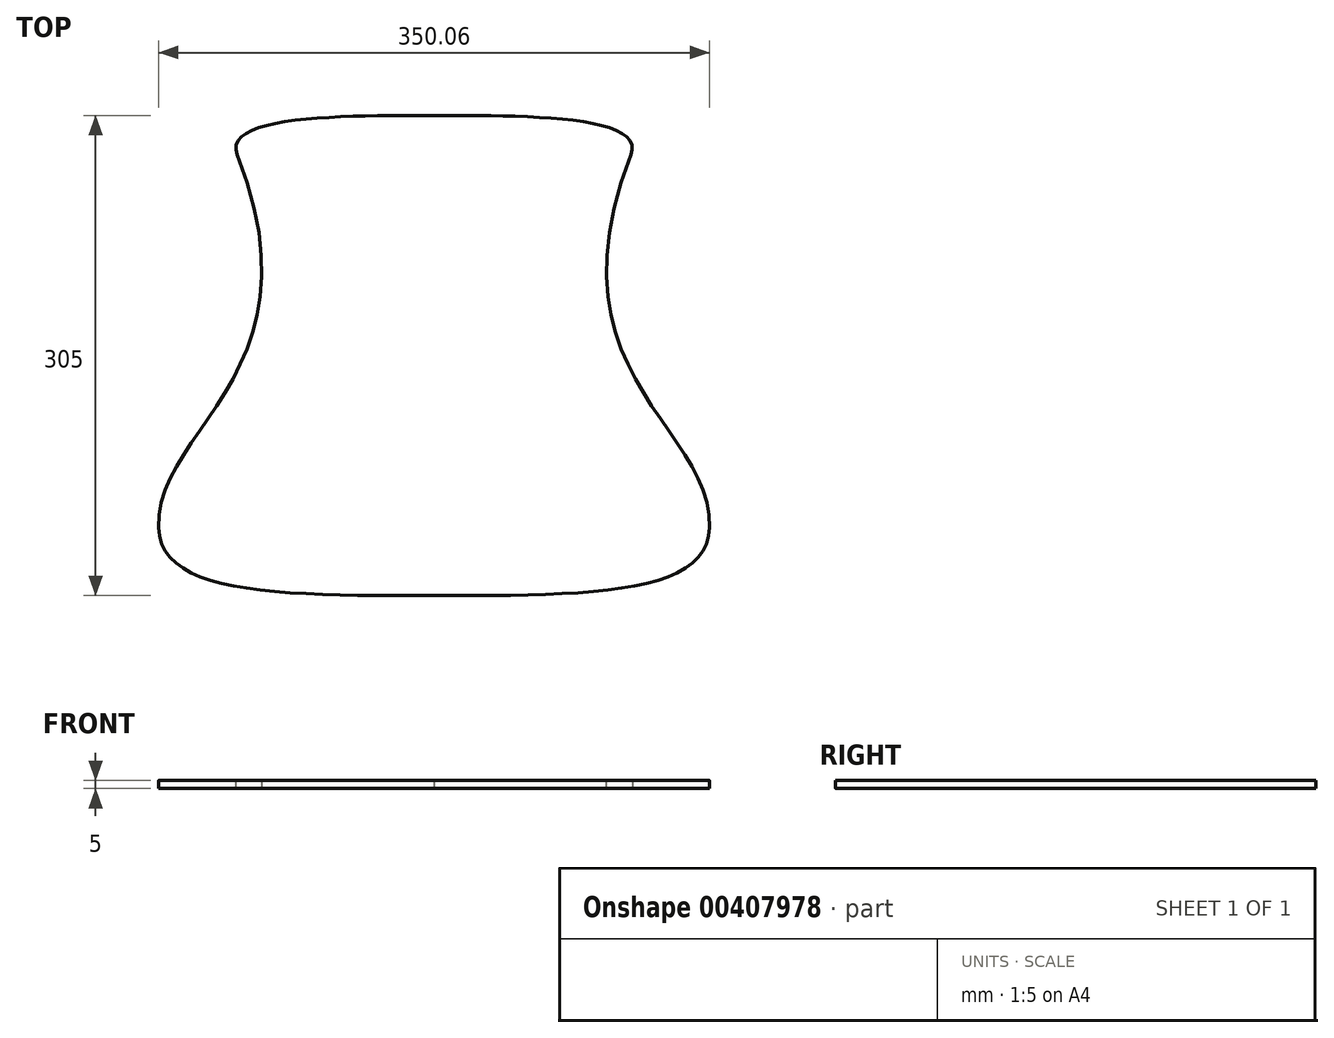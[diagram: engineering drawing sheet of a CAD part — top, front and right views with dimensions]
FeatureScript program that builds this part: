
annotation { "Feature Type Name" : "Feature", "Feature Type Description" : "" }
export const myFeature = defineFeature(function(context is Context, id is Id, definition is map)
    precondition{}
    {
        {
            var Q0;
            Q0=qCreatedBy(makeId("Top.planeOp"),FACE);
            var sketch = newSketch(context, id + "F0", { "sketchPlane" : qUnion([Q0])});
            skLineSegment(sketch, "E0.bottom", {"start": v(-125, 0) * mm, "end": v(125, 0) * mm, "construction": true});
            skLineSegment(sketch, "E0.top", {"start": v(-125, -280) * mm, "end": v(125, -280) * mm, "construction": true});
            skLineSegment(sketch, "E0.left", {"start": v(-125, 0) * mm, "end": v(-125, -280) * mm, "construction": true});
            skLineSegment(sketch, "E0.right", {"start": v(125, 0) * mm, "end": v(125, -280) * mm, "construction": true});
            skFitSpline(sketch, "E1", {"points": [v(-125, 0) * mm, v(-175, -236.88) * mm], "startDerivative": vector(163.58, -419.06) * mm, "endDerivative": vector(5.98, -192.46) * mm});
            skPoint(sketch, "E2", {"position": v(0, -280) * mm});
            skFitSpline(sketch, "E3", {"points": [v(-175, -236.88) * mm, v(0, -280) * mm], "startDerivative": vector(4.02, -129.37) * mm, "endDerivative": vector(290.73, 0) * mm});
            skFitSpline(sketch, "E4.MirrorCS", {"points": [v(125, 0) * mm, v(175, -236.88) * mm], "startDerivative": vector(-163.58, -419.06) * mm, "endDerivative": vector(-5.98, -192.46) * mm});
            skFitSpline(sketch, "E5.MirrorCS", {"points": [v(175, -236.88) * mm, v(0, -280) * mm], "startDerivative": vector(-4.02, -129.37) * mm, "endDerivative": vector(-290.73, 0) * mm});
            skFitSpline(sketch, "E6", {"points": [v(-125, 0) * mm, v(0, 25) * mm], "startDerivative": vector(-31, 79.42) * mm, "endDerivative": vector(148.36, 0.98) * mm});
            skFitSpline(sketch, "E7.MirrorCS", {"points": [v(125, 0) * mm, v(0, 25) * mm], "startDerivative": vector(31, 79.42) * mm, "endDerivative": vector(-148.36, 0.98) * mm});
            skLineSegment(sketch, "E8.bottom", {"start": v(-10, -88) * mm, "end": v(-5, -88) * mm, "construction": true});
            skLineSegment(sketch, "E8.top", {"start": v(-10, -278) * mm, "end": v(-5, -278) * mm, "construction": true});
            skLineSegment(sketch, "E8.left", {"start": v(-10, -88) * mm, "end": v(-10, -278) * mm, "construction": true});
            skLineSegment(sketch, "E8.right", {"start": v(-5, -88) * mm, "end": v(-5, -278) * mm, "construction": true});
            skLineSegment(sketch, "E9.1.0.0", {"start": v(-20, -88) * mm, "end": v(-20, -278) * mm, "construction": true});
            skLineSegment(sketch, "E9.1.0.1", {"start": v(-15, -88) * mm, "end": v(-15, -278) * mm, "construction": true});
            skLineSegment(sketch, "E9.1.0.2", {"start": v(-20, -88) * mm, "end": v(-15, -88) * mm, "construction": true});
            skLineSegment(sketch, "E9.1.0.3", {"start": v(-20, -278) * mm, "end": v(-15, -278) * mm, "construction": true});
            skLineSegment(sketch, "E9.2.0.0", {"start": v(-30, -88) * mm, "end": v(-30, -278) * mm, "construction": true});
            skLineSegment(sketch, "E9.2.0.1", {"start": v(-25, -88) * mm, "end": v(-25, -278) * mm, "construction": true});
            skLineSegment(sketch, "E9.2.0.2", {"start": v(-30, -88) * mm, "end": v(-25, -88) * mm, "construction": true});
            skLineSegment(sketch, "E9.2.0.3", {"start": v(-30, -278) * mm, "end": v(-25, -278) * mm, "construction": true});
            skLineSegment(sketch, "E9.direction1", {"start": v(-10, -278) * mm, "end": v(-20, -278) * mm, "construction": true});
            skLineSegment(sketch, "E10.MirrorCS", {"start": v(10, -278) * mm, "end": v(20, -278) * mm, "construction": true});
            skLineSegment(sketch, "E11.MirrorCS", {"start": v(20, -278) * mm, "end": v(15, -278) * mm, "construction": true});
            skLineSegment(sketch, "E12.MirrorCS", {"start": v(10, -278) * mm, "end": v(5, -278) * mm, "construction": true});
            skLineSegment(sketch, "E13.MirrorCS", {"start": v(20, -88) * mm, "end": v(15, -88) * mm, "construction": true});
            skLineSegment(sketch, "E14.MirrorCS", {"start": v(30, -278) * mm, "end": v(25, -278) * mm, "construction": true});
            skLineSegment(sketch, "E15.MirrorCS", {"start": v(10, -88) * mm, "end": v(5, -88) * mm, "construction": true});
            skLineSegment(sketch, "E16.MirrorCS", {"start": v(30, -88) * mm, "end": v(25, -88) * mm, "construction": true});
            skLineSegment(sketch, "E17.MirrorCS", {"start": v(30, -88) * mm, "end": v(30, -278) * mm, "construction": true});
            skLineSegment(sketch, "E18.MirrorCS", {"start": v(10, -88) * mm, "end": v(10, -278) * mm, "construction": true});
            skLineSegment(sketch, "E19.MirrorCS", {"start": v(15, -88) * mm, "end": v(15, -278) * mm, "construction": true});
            skLineSegment(sketch, "E20.MirrorCS", {"start": v(5, -88) * mm, "end": v(5, -278) * mm, "construction": true});
            skLineSegment(sketch, "E21.MirrorCS", {"start": v(20, -88) * mm, "end": v(20, -278) * mm, "construction": true});
            skLineSegment(sketch, "E22.MirrorCS", {"start": v(25, -88) * mm, "end": v(25, -278) * mm, "construction": true});
            skLineSegment(sketch, "E23.bottom", {"start": v(-73, -5) * mm, "end": v(-57, -5) * mm, "construction": true});
            skLineSegment(sketch, "E23.top", {"start": v(-73, -18) * mm, "end": v(-57, -18) * mm, "construction": true});
            skLineSegment(sketch, "E23.left", {"start": v(-73, -5) * mm, "end": v(-73, -18) * mm, "construction": true});
            skLineSegment(sketch, "E23.right", {"start": v(-57, -5) * mm, "end": v(-57, -18) * mm, "construction": true});
            skCircle(sketch, "E24", {"center": v(-73, -5) * mm, "radius": 2.02 * mm, "construction": true});
            skCircle(sketch, "E25", {"center": v(-57, -5) * mm, "radius": 2.02 * mm, "construction": true});
            skCircle(sketch, "E26", {"center": v(-57, -18) * mm, "radius": 2.02 * mm, "construction": true});
            skCircle(sketch, "E27", {"center": v(-73, -18) * mm, "radius": 2.02 * mm, "construction": true});
            skPoint(sketch, "E28", {"position": v(-65, -5) * mm});
            skLineSegment(sketch, "E29.MirrorCS", {"start": v(73, -18) * mm, "end": v(57, -18) * mm, "construction": true});
            skCircle(sketch, "E30.MirrorC", {"center": v(57, -5) * mm, "radius": 2.02 * mm, "construction": true});
            skCircle(sketch, "E31.MirrorC", {"center": v(57, -18) * mm, "radius": 2.02 * mm, "construction": true});
            skPoint(sketch, "E32.MirrorP", {"position": v(65, -5) * mm});
            skCircle(sketch, "E33.MirrorC", {"center": v(73, -5) * mm, "radius": 2.02 * mm, "construction": true});
            skLineSegment(sketch, "E34.MirrorCS", {"start": v(73, -5) * mm, "end": v(57, -5) * mm, "construction": true});
            skLineSegment(sketch, "E35.MirrorCS", {"start": v(57, -5) * mm, "end": v(57, -18) * mm, "construction": true});
            skCircle(sketch, "E36.MirrorC", {"center": v(73, -18) * mm, "radius": 2.02 * mm, "construction": true});
            skLineSegment(sketch, "E37.MirrorCS", {"start": v(73, -5) * mm, "end": v(73, -18) * mm, "construction": true});
            skSolve(sketch);
        }
        {
            var Q0;
            Q0 = qSketchRegion(id + "F0", true);
            extrude(context, id + "F1", {"entities" : qUnion([Q0]), "depth" : 5 * mm});
        }
    });
